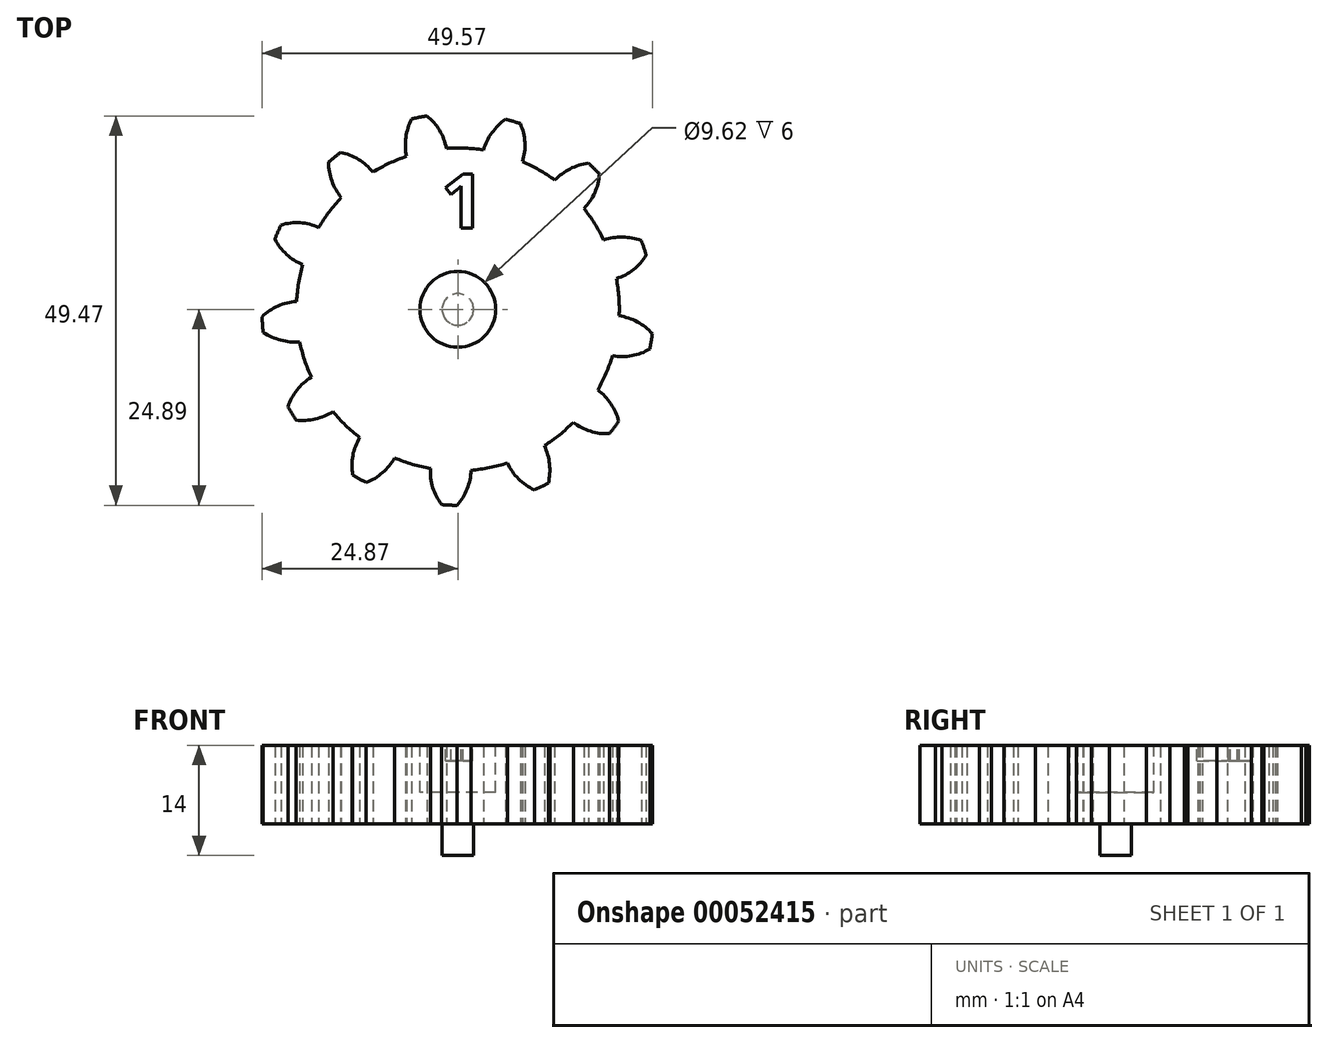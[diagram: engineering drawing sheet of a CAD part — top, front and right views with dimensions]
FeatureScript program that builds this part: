
annotation { "Feature Type Name" : "Feature", "Feature Type Description" : "" }
export const myFeature = defineFeature(function(context is Context, id is Id, definition is map)
    precondition{}
    {
        {
            var Q0;
            Q0=qCreatedBy(makeId("Top.planeOp"),FACE);
            var sketch = newSketch(context, id + "F0", { "sketchPlane" : qUnion([Q0])});
            skCircle(sketch, "E0", {"center": v(0, 0) * mm, "radius": 25.4 * mm, "construction": true});
            skCircle(sketch, "E1", {"center": v(0, 0) * mm, "radius": 24.9 * mm});
            skCircle(sketch, "E2", {"center": v(0, 0) * mm, "radius": 22.13 * mm, "construction": true});
            skCircle(sketch, "E3", {"center": v(0, 0) * mm, "radius": 20.9 * mm, "construction": true});
            skLineSegment(sketch, "E4", {"start": v(0, 20.9) * mm, "end": v(0, 25.4) * mm, "construction": true});
            skLineSegment(sketch, "E5", {"start": v(-6.36, 24.6) * mm, "end": v(-5.23, 20.23) * mm, "construction": true});
            skLineSegment(sketch, "E6", {"start": v(-5.23, 20.23) * mm, "end": v(0, 22.13) * mm, "construction": true});
            skLineSegment(sketch, "E7", {"start": v(-13.83, 20.7) * mm, "end": v(-14.11, 21.12) * mm});
            skLineSegment(sketch, "E8", {"start": v(0, 22.13) * mm, "end": v(6.62, 24.52) * mm, "construction": true});
            skLineSegment(sketch, "E9", {"start": v(10.24, 18.22) * mm, "end": v(3.9, 21.78) * mm, "construction": true});
            skCircle(sketch, "E10", {"center": v(10.24, 18.22) * mm, "radius": 7.26 * mm});
            skLineSegment(sketch, "E11", {"start": v(3.9, 21.78) * mm, "end": v(4.4, 24.5) * mm, "construction": true});
            skLineSegment(sketch, "E12", {"start": v(15.28, 19.65) * mm, "end": v(13.58, 17.47) * mm, "construction": true});
            skLineSegment(sketch, "E13", {"start": v(10.13, 22.74) * mm, "end": v(9, 20.21) * mm, "construction": true});
            skLineSegment(sketch, "E14", {"start": v(3.9, 21.78) * mm, "end": v(10.13, 22.74) * mm, "construction": true});
            skLineSegment(sketch, "E15", {"start": v(13.58, 17.47) * mm, "end": v(10.13, 22.74) * mm, "construction": true});
            skCircle(sketch, "E16", {"center": v(0, 0) * mm, "radius": 20.5 * mm});
            skLineSegment(sketch, "E17", {"start": v(5.68, 19.55) * mm, "end": v(3.26, 20.25) * mm, "construction": true});
            skLineSegment(sketch, "E18", {"start": v(9, 20.21) * mm, "end": v(8.5, 20.25) * mm});
            skLineSegment(sketch, "E19", {"start": v(8.5, 20.25) * mm, "end": v(1.77, 20.83) * mm, "construction": true});
            skCircle(sketch, "E20", {"center": v(1.77, 20.83) * mm, "radius": 6.76 * mm});
            skLineSegment(sketch, "E21", {"start": v(5.68, 19.55) * mm, "end": v(7.21, 24.82) * mm, "construction": true});
            skLineSegment(sketch, "E22", {"start": v(9, 20.21) * mm, "end": v(3.9, 21.78) * mm, "construction": true});
            skSolve(sketch);
        }
        {
            var Q0;
            {var subQ0=sQuery(id+"F0.wireOp",EDGE,"E20");var subQ3=sQuery(id+"F0.wireOp",EDGE,"E10");var subQ4=makeQuery(id+"F0.imprint","INTERSECT",VERTEX,{"disambiguationData":[OD(1.0)],"derivedFrom":[subQ3,subQ0]});Q0=makeQuery(id+"F0.imprint","IMPRINT",FACE,{"disambiguationData":[TD([[makeQuery(id+"F0.imprint","IMPRINT",EDGE,{"disambiguationData":[TD([[subQ4,-1.0]])],"derivedFrom":subQ3}),-1.0]])]});}
            var Q1;
            {var subQ0=sQuery(id+"F0.wireOp",EDGE,"E20");var subQ3=sQuery(id+"F0.wireOp",EDGE,"E10");var subQ4=makeQuery(id+"F0.imprint","INTERSECT",VERTEX,{"disambiguationData":[OD(1.0)],"derivedFrom":[subQ3,subQ0]});Q1=makeQuery(id+"F0.imprint","IMPRINT",FACE,{"disambiguationData":[TD([[makeQuery(id+"F0.imprint","IMPRINT",EDGE,{"disambiguationData":[TD([[subQ4,-1.0]])],"derivedFrom":subQ3}),1.0]])]});}
            var Q2;
            {var subQ1=sQuery(id+"F0.wireOp",EDGE,"E16");var subQ3=sQuery(id+"F0.wireOp",EDGE,"E10");var subQ5=makeQuery(id+"F0.imprint","INTERSECT",VERTEX,{"disambiguationData":[OD(0.0)],"derivedFrom":[subQ3,subQ1]});Q2=makeQuery(id+"F0.imprint","IMPRINT",FACE,{"disambiguationData":[TD([[makeQuery(id+"F0.imprint","IMPRINT",EDGE,{"disambiguationData":[TD([[subQ5,-1.0]])],"derivedFrom":subQ3}),1.0]])]});}
            var Q3;
            {var subQ1=sQuery(id+"F0.wireOp",EDGE,"E16");var subQ3=sQuery(id+"F0.wireOp",EDGE,"E10");var subQ5=makeQuery(id+"F0.imprint","INTERSECT",VERTEX,{"disambiguationData":[OD(0.0)],"derivedFrom":[subQ3,subQ1]});Q3=makeQuery(id+"F0.imprint","IMPRINT",FACE,{"disambiguationData":[TD([[makeQuery(id+"F0.imprint","IMPRINT",EDGE,{"disambiguationData":[TD([[subQ5,-1.0]])],"derivedFrom":subQ3}),-1.0]])]});}
            var Q4;
            {var subQ0=sQuery(id+"F0.wireOp",EDGE,"E20");var subQ3=makeQuery(id+"F0.imprint","IMPRINT",VERTEX,{"derivedFrom":subQ0});Q4=makeQuery(id+"F0.imprint","IMPRINT",FACE,{"disambiguationData":[TD([[makeQuery(id+"F0.imprint","IMPRINT",EDGE,{"disambiguationData":[TD([[subQ3,-1.0]])],"derivedFrom":subQ0}),1.0]])]});}
            extrude(context, id + "F1", {"entities" : qUnion([Q0, Q1, Q2, Q3, Q4]), "depth" : 10 * mm});
        }
        {
            var Q0;
            Q0=makeQuery(id+"F1.opExtrude","SWEPT_BODY",BODY,{"disambiguationData":[OSD([sQuery(id+"F0.wireOp",EDGE,"E1"),sQuery(id+"F0.wireOp",EDGE,"E10"),sQuery(id+"F0.wireOp",EDGE,"E16"),sQuery(id+"F0.wireOp",EDGE,"E20")])]});
            var Q1;
            Q1=makeQuery(id+"F1.opExtrude","CAP_EDGE",EDGE,{"disambiguationData":[OSD([sQuery(id+"F0.wireOp",EDGE,"E16")])],"isStart":false});
            circularPattern(context, id + "F2", {"operationType" : NewBodyOperationType.ADD, "entities" : qUnion([Q0]), "axis" : qUnion([Q1]), "angle" : 360 * degree, "instanceCount" : round(13), "equalSpace" : true});
        }
        {
            var Q0;
            {var subQ0=makeQuery(id+"F1.opExtrude","CAP_FACE",FACE,{"disambiguationData":[OSD([sQuery(id+"F0.wireOp",EDGE,"E1"),sQuery(id+"F0.wireOp",EDGE,"E10"),sQuery(id+"F0.wireOp",EDGE,"E16"),sQuery(id+"F0.wireOp",EDGE,"E20")])],"isStart":false});Q0=makeQuery(id+"F2.boolean.opBoolean","MERGE",FACE,{"derivedFrom":[subQ0,makeQuery(id+"F2.opPattern","COPY",FACE,{"derivedFrom":subQ0,"instanceName":"1"}),makeQuery(id+"F2.opPattern","COPY",FACE,{"derivedFrom":subQ0,"instanceName":"2"}),makeQuery(id+"F2.opPattern","COPY",FACE,{"derivedFrom":subQ0,"instanceName":"3"}),makeQuery(id+"F2.opPattern","COPY",FACE,{"derivedFrom":subQ0,"instanceName":"4"}),makeQuery(id+"F2.opPattern","COPY",FACE,{"derivedFrom":subQ0,"instanceName":"5"}),makeQuery(id+"F2.opPattern","COPY",FACE,{"derivedFrom":subQ0,"instanceName":"6"}),makeQuery(id+"F2.opPattern","COPY",FACE,{"derivedFrom":subQ0,"instanceName":"7"}),makeQuery(id+"F2.opPattern","COPY",FACE,{"derivedFrom":subQ0,"instanceName":"8"}),makeQuery(id+"F2.opPattern","COPY",FACE,{"derivedFrom":subQ0,"instanceName":"9"}),makeQuery(id+"F2.opPattern","COPY",FACE,{"derivedFrom":subQ0,"instanceName":"10"}),makeQuery(id+"F2.opPattern","COPY",FACE,{"derivedFrom":subQ0,"instanceName":"11"}),makeQuery(id+"F2.opPattern","COPY",FACE,{"derivedFrom":subQ0,"instanceName":"12"})]});}
            var sketch = newSketch(context, id + "F3", { "sketchPlane" : qUnion([Q0])});
            skPoint(sketch, "E23.rect.middle", {"position": v(0, 14.76) * mm});
            skCircle(sketch, "E24.0", {"center": v(0, 0) * mm, "radius": 4.81 * mm});
            skSolve(sketch);
        }
        {
            var Q0;
            Q0=makeQuery(id+"F3.imprint","IMPRINT",FACE,{"disambiguationData":[TD([[makeQuery(id+"F3.imprint","IMPRINT",EDGE,{"derivedFrom":sQuery(id+"F3.wireOp",EDGE,"E24.0")}),1.0]])]});
            extrude(context, id + "F4", {"entities" : qUnion([Q0]), "operationType" : NewBodyOperationType.REMOVE, "oppositeDirection" : true, "depth" : 6 * mm});
        }
        {
            var Q0;
            {var subQ0=makeQuery(id+"F1.opExtrude","CAP_FACE",FACE,{"disambiguationData":[OSD([sQuery(id+"F0.wireOp",EDGE,"E1"),sQuery(id+"F0.wireOp",EDGE,"E10"),sQuery(id+"F0.wireOp",EDGE,"E16"),sQuery(id+"F0.wireOp",EDGE,"E20")])],"isStart":true});Q0=makeQuery(id+"F2.boolean.opBoolean","MERGE",FACE,{"derivedFrom":[subQ0,makeQuery(id+"F2.opPattern","COPY",FACE,{"derivedFrom":subQ0,"instanceName":"1"}),makeQuery(id+"F2.opPattern","COPY",FACE,{"derivedFrom":subQ0,"instanceName":"2"}),makeQuery(id+"F2.opPattern","COPY",FACE,{"derivedFrom":subQ0,"instanceName":"3"}),makeQuery(id+"F2.opPattern","COPY",FACE,{"derivedFrom":subQ0,"instanceName":"4"}),makeQuery(id+"F2.opPattern","COPY",FACE,{"derivedFrom":subQ0,"instanceName":"5"}),makeQuery(id+"F2.opPattern","COPY",FACE,{"derivedFrom":subQ0,"instanceName":"6"}),makeQuery(id+"F2.opPattern","COPY",FACE,{"derivedFrom":subQ0,"instanceName":"7"}),makeQuery(id+"F2.opPattern","COPY",FACE,{"derivedFrom":subQ0,"instanceName":"8"}),makeQuery(id+"F2.opPattern","COPY",FACE,{"derivedFrom":subQ0,"instanceName":"9"}),makeQuery(id+"F2.opPattern","COPY",FACE,{"derivedFrom":subQ0,"instanceName":"10"}),makeQuery(id+"F2.opPattern","COPY",FACE,{"derivedFrom":subQ0,"instanceName":"11"}),makeQuery(id+"F2.opPattern","COPY",FACE,{"derivedFrom":subQ0,"instanceName":"12"})]});}
            var sketch = newSketch(context, id + "F5", { "sketchPlane" : qUnion([Q0])});
            skCircle(sketch, "E25", {"center": v(0, 0) * mm, "radius": 2 * mm});
            skSolve(sketch);
        }
        {
            var Q0;
            Q0 = qSketchRegion(id + "F5", true);
            extrude(context, id + "F6", {"entities" : qUnion([Q0]), "operationType" : NewBodyOperationType.ADD, "depth" : 4 * mm});
        }
        {
            var Q0;
            {var subQ0=makeQuery(id+"F1.opExtrude","CAP_FACE",FACE,{"disambiguationData":[OSD([sQuery(id+"F0.wireOp",EDGE,"E1"),sQuery(id+"F0.wireOp",EDGE,"E10"),sQuery(id+"F0.wireOp",EDGE,"E16"),sQuery(id+"F0.wireOp",EDGE,"E20")])],"isStart":false});Q0=makeQuery(id+"F2.boolean.opBoolean","MERGE",FACE,{"derivedFrom":[subQ0,makeQuery(id+"F2.opPattern","COPY",FACE,{"derivedFrom":subQ0,"instanceName":"1"}),makeQuery(id+"F2.opPattern","COPY",FACE,{"derivedFrom":subQ0,"instanceName":"2"}),makeQuery(id+"F2.opPattern","COPY",FACE,{"derivedFrom":subQ0,"instanceName":"3"}),makeQuery(id+"F2.opPattern","COPY",FACE,{"derivedFrom":subQ0,"instanceName":"4"}),makeQuery(id+"F2.opPattern","COPY",FACE,{"derivedFrom":subQ0,"instanceName":"5"}),makeQuery(id+"F2.opPattern","COPY",FACE,{"derivedFrom":subQ0,"instanceName":"6"}),makeQuery(id+"F2.opPattern","COPY",FACE,{"derivedFrom":subQ0,"instanceName":"7"}),makeQuery(id+"F2.opPattern","COPY",FACE,{"derivedFrom":subQ0,"instanceName":"8"}),makeQuery(id+"F2.opPattern","COPY",FACE,{"derivedFrom":subQ0,"instanceName":"9"}),makeQuery(id+"F2.opPattern","COPY",FACE,{"derivedFrom":subQ0,"instanceName":"10"}),makeQuery(id+"F2.opPattern","COPY",FACE,{"derivedFrom":subQ0,"instanceName":"11"}),makeQuery(id+"F2.opPattern","COPY",FACE,{"derivedFrom":subQ0,"instanceName":"12"})]});}
            var sketch = newSketch(context, id + "F7", { "sketchPlane" : qUnion([Q0])});
            skText(sketch, "E26", { "text": "1", "fontName": "OpenSans-Bold.ttf"});
            skPoint(sketch, "E27.start.orphan", {"position": v(0, 0) * mm});
            const initialGuessF7  = {"E26": [-0.00215, 0.01031, 1, 0, 0.00697]};
            skSetInitialGuess(sketch, initialGuessF7);
            skSolve(sketch);
        }
        {
            var Q0;
            Q0 = qSketchRegion(id + "F7", true);
            extrude(context, id + "F8", {"entities" : qUnion([Q0]), "operationType" : NewBodyOperationType.REMOVE, "oppositeDirection" : true, "depth" : 2 * mm});
        }
    });
